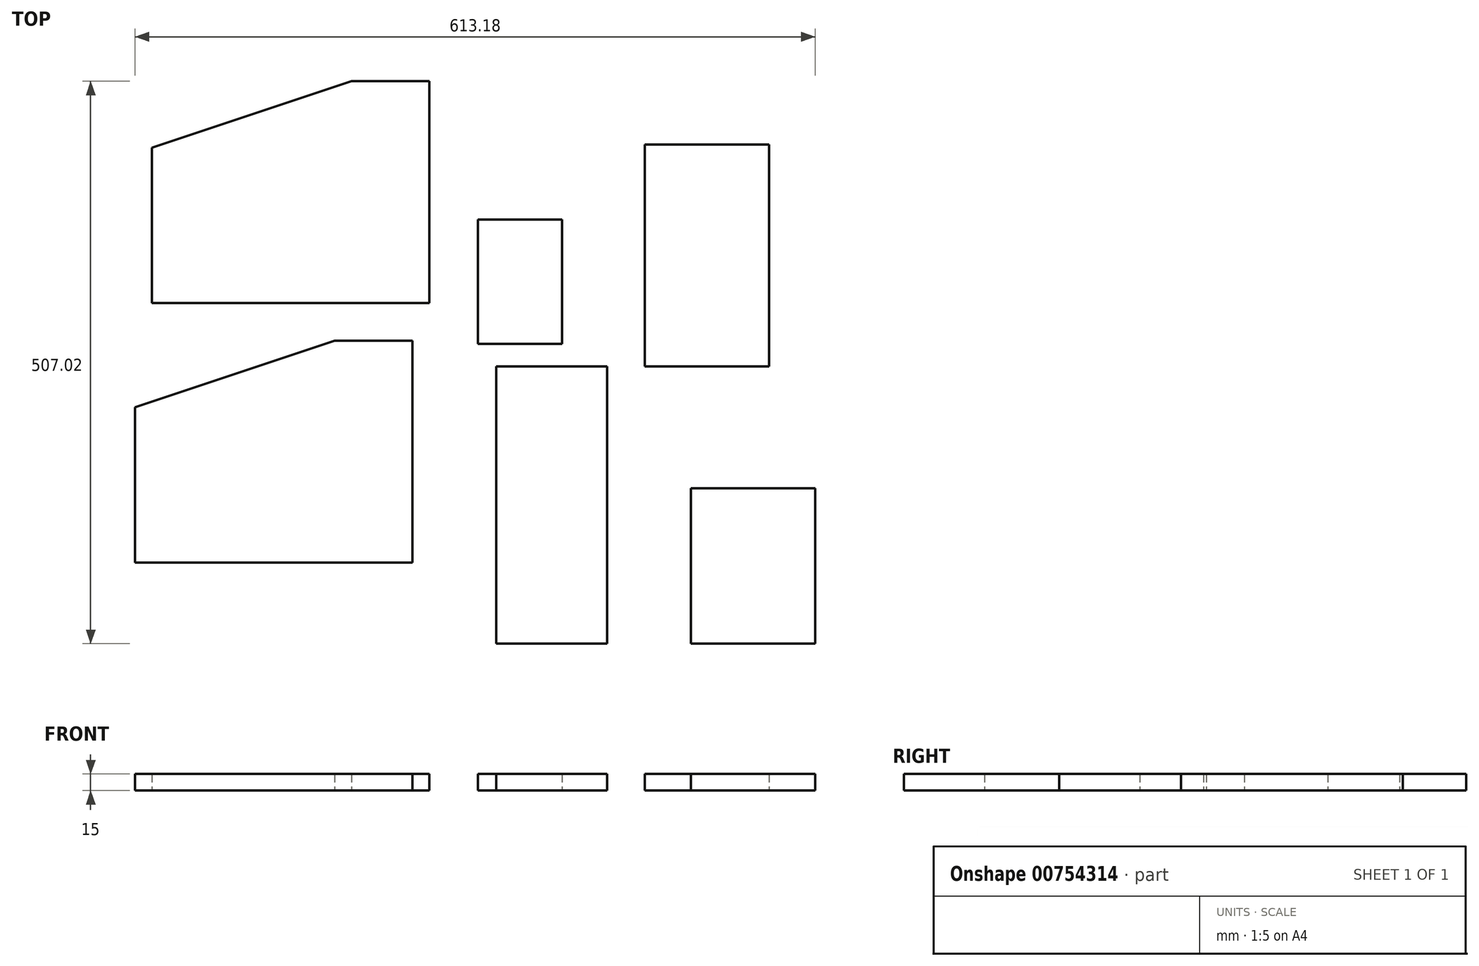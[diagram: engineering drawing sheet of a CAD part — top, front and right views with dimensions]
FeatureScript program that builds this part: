
annotation { "Feature Type Name" : "Feature", "Feature Type Description" : "" }
export const myFeature = defineFeature(function(context is Context, id is Id, definition is map)
    precondition{}
    {
        {
            var Q0;
            Q0=qCreatedBy(makeId("Top.planeOp"),FACE);
            var sketch = newSketch(context, id + "F0", { "sketchPlane" : qUnion([Q0])});
            skLineSegment(sketch, "E0.right", {"start": v(-43.93, 37) * mm, "end": v(-43.93, 3.55) * mm});
            skLineSegment(sketch, "E1.bottom", {"start": v(-9.9, 237) * mm, "end": v(102.1, 237) * mm});
            skLineSegment(sketch, "E1.top", {"start": v(-9.9, 37) * mm, "end": v(102.1, 37) * mm});
            skLineSegment(sketch, "E1.left", {"start": v(-9.9, 237) * mm, "end": v(-9.9, 37) * mm});
            skLineSegment(sketch, "E1.right", {"start": v(102.1, 237) * mm, "end": v(102.1, 37) * mm});
            skPoint(sketch, "E2.firstSnap0", {"position": v(46.1, 37) * mm});
            skLineSegment(sketch, "E2.bottom", {"start": v(-143.93, 37) * mm, "end": v(-43.93, 37) * mm});
            skLineSegment(sketch, "E2.top", {"start": v(-143.93, -213) * mm, "end": v(-43.93, -213) * mm});
            skLineSegment(sketch, "E2.left", {"start": v(-143.93, 37) * mm, "end": v(-143.93, -213) * mm});
            skLineSegment(sketch, "E2.right", {"start": v(-43.93, 3.55) * mm, "end": v(-43.93, -213) * mm});
            skLineSegment(sketch, "E3.bottom", {"start": v(31.74, -73) * mm, "end": v(143.74, -73) * mm});
            skLineSegment(sketch, "E3.top", {"start": v(31.74, -213) * mm, "end": v(143.74, -213) * mm});
            skLineSegment(sketch, "E3.left", {"start": v(31.74, -73) * mm, "end": v(31.74, -213) * mm});
            skLineSegment(sketch, "E3.right", {"start": v(143.74, -73) * mm, "end": v(143.74, -213) * mm});
            skLineSegment(sketch, "E4.bottom", {"start": v(-160.44, 169.3) * mm, "end": v(-84.44, 169.3) * mm});
            skLineSegment(sketch, "E4.top", {"start": v(-160.44, 57.3) * mm, "end": v(-84.44, 57.3) * mm});
            skLineSegment(sketch, "E4.left", {"start": v(-160.44, 169.3) * mm, "end": v(-160.44, 57.3) * mm});
            skLineSegment(sketch, "E4.right", {"start": v(-84.44, 169.3) * mm, "end": v(-84.44, 57.3) * mm});
            skLineSegment(sketch, "E5", {"start": v(-289.44, 60) * mm, "end": v(-219.44, 60) * mm});
            skLineSegment(sketch, "E6", {"start": v(-219.44, 60) * mm, "end": v(-219.44, -140) * mm});
            skLineSegment(sketch, "E7", {"start": v(-219.44, -140) * mm, "end": v(-469.44, -140) * mm});
            skLineSegment(sketch, "E8", {"start": v(-469.44, -140) * mm, "end": v(-469.44, 0) * mm});
            skLineSegment(sketch, "E9", {"start": v(-289.44, 60) * mm, "end": v(-469.44, 0) * mm});
            skLineSegment(sketch, "E10", {"start": v(-274.2, 294.03) * mm, "end": v(-204.2, 294.03) * mm});
            skLineSegment(sketch, "E11", {"start": v(-204.2, 294.03) * mm, "end": v(-204.2, 94.03) * mm});
            skLineSegment(sketch, "E12", {"start": v(-204.2, 94.03) * mm, "end": v(-454.2, 94.03) * mm});
            skLineSegment(sketch, "E13", {"start": v(-454.2, 94.03) * mm, "end": v(-454.2, 234.03) * mm});
            skLineSegment(sketch, "E14", {"start": v(-274.2, 294.03) * mm, "end": v(-454.2, 234.03) * mm});
            skSolve(sketch);
        }
        {
            var Q0;
            Q0 = qSketchRegion(id + "F0", true);
            extrude(context, id + "F1", {"entities" : qUnion([Q0]), "depth" : 15 * mm, "offsetDistance" : 25 * mm});
        }
    });
